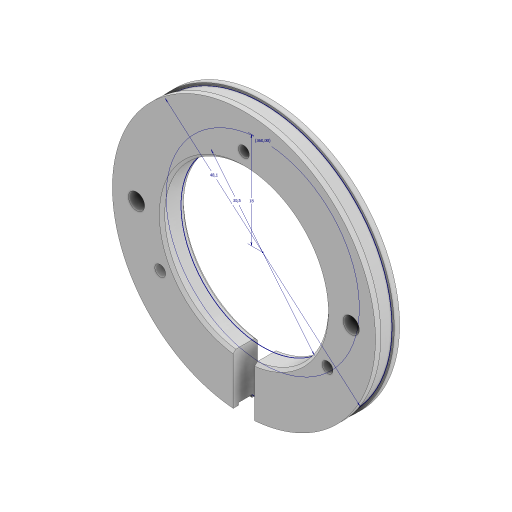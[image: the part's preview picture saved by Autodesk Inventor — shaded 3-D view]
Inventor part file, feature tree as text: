
AUTODESK INVENTOR PART (.ipt)
format: ipt  version: 2023 (Build 270158000, 158)  size: 189,440 bytes
history: native  units: mm
features: sketch x5, extrude x4, hole x2, chamfer x1
ambient origin geometry x8: Origin, YZ Plane, XZ Plane, XY Plane, X Axis, Y Axis, Z Axis, Center Point
bodies: Solid1 (feature_tree)
feature tree (12):
  sketch  "Sketch1"  dims[d0=30.5mm d1=48.1mm]
  extrude  "Extrusion1"  Depth=48.1mm
  hole  "Hole1"  [1 undecoded]
  extrude  "Extrusion2"  Depth=49.0mm
  extrude  "Extrusion3"  Depth=1.0mm TaperAngle=0.0deg
  extrude  "Extrusion4"  Depth=1.0mm
  hole  "Hole2"  [1 undecoded]
  chamfer  "Chamfer1"  Distance=20.0mm
  sketch  "Sketch2"  dims[d2=18.0mm d3=30.0mm d5=360.0deg]
  sketch  "Sketch3"  dims[d7=2.5mm d8=0.0mm]
  sketch  "Sketch4"  dims[d9=2.0mm d10=6.0mm d11=4.0mm d12=2.0mm d13=90.0deg d14=8.0mm d15=20.594885mm d16=49.0mm]
  sketch  "Sketch5"  dims[d17=1.0mm d18=0.0mm d19=1.0mm d20=0.0mm d21=49.0mm d22=4.0mm d23=20.0mm d24=0.0mm d25=0.0mm d26=3.0mm d27=6.0mm d28=4.0mm d29=2.0mm d30=90.0deg d31=8.0mm d32=20.594885mm d33=0.0mm d34=0.5mm d35=2.0mm d36=45.0deg]
note: 2 required parameter values undecoded (feature->parameter linkage not recoverable at this tier; creation-order binding heuristic only, values carry confidence <= 0.55)
